annotation { "Feature Type Name" : "Feature", "Feature Type Description" : "" }
export const myFeature = defineFeature(function(context is Context, id is Id, definition is map)
    precondition{}
    {
        {
            var Q0;
            Q0=qCreatedBy(makeId("Front.planeOp"),FACE);
            var sketch = newSketch(context, id + "F0", { "sketchPlane" : qUnion([Q0])});
            skLineSegment(sketch, "E0.bottom", {"start": v(-65.9, -69.94) * mm, "end": v(59.04, -69.94) * mm});
            skLineSegment(sketch, "E0.top", {"start": v(-15.1, 77.26) * mm, "end": v(8.24, 77.26) * mm});
            skLineSegment(sketch, "E0.left", {"start": v(-65.9, -69.94) * mm, "end": v(-65.9, 26.46) * mm});
            skLineSegment(sketch, "E0.right", {"start": v(59.04, -69.94) * mm, "end": v(59.04, 26.46) * mm});
            skPoint(sketch, "E1.visualSharp", {"position": v(-65.9, 77.26) * mm});
            skArc(sketch, "E1.filletArc", {"start": v(-15.1, 77.26) * mm, "mid": v(-51.03, 62.38) * mm, "end": v(-65.9, 26.46) * mm});
            skPoint(sketch, "E2.visualSharp", {"position": v(59.04, 77.26) * mm});
            skArc(sketch, "E2.filletArc", {"start": v(59.04, 26.46) * mm, "mid": v(44.16, 62.38) * mm, "end": v(8.24, 77.26) * mm});
            skLineSegment(sketch, "E3.bottom", {"start": v(-44.34, 56.46) * mm, "end": v(37.67, 56.46) * mm});
            skLineSegment(sketch, "E3.top", {"start": v(-44.34, 28.64) * mm, "end": v(37.67, 28.64) * mm});
            skLineSegment(sketch, "E3.left", {"start": v(-44.34, 56.46) * mm, "end": v(-44.34, 28.64) * mm});
            skLineSegment(sketch, "E3.right", {"start": v(37.67, 56.46) * mm, "end": v(37.67, 28.64) * mm});
            skText(sketch, "E4", { "text": "EUGENE SMITH", "fontName": "OpenSans-Bold.ttf"});
            skText(sketch, "E5", { "text": "1111 - 2222", "fontName": "Arimo-Regular.ttf"});
            const initialGuessF0  = {"E4": [-0.04202, 0.0385, 1, 0, 0.00753], "E5": [-0.04434, -0.03222, 1, 0, 0.01102]};
            skSetInitialGuess(sketch, initialGuessF0);
            skSolve(sketch);
        }
        {
            var Q0;
            Q0=makeQuery(id+"F0.imprint","IMPRINT",FACE,{"disambiguationData":[TD([[makeQuery(id+"F0.imprint","IMPRINT",EDGE,{"derivedFrom":sQuery(id+"F0.wireOp",EDGE,"E3.bottom")}),-1.0]])]});
            extrude(context, id + "F1", {"entities" : qUnion([Q0]), "depth" : 50.8 * mm});
        }
        {
            var Q0;
            Q0 = qSketchRegion(id + "F0", true);
            extrude(context, id + "F2", {"entities" : qUnion([Q0]), "operationType" : NewBodyOperationType.ADD, "depth" : 38.1 * mm});
        }
    });